# Revit family: Shower-Handshower-KOHLER-Statement-K-20998T_1
name_source: partatom
category: Plumbing Fixtures
units: mm (PartAtom-declared; Revit-internal decimal feet)

## family parameters
Cut with Voids When Loaded = No
Host = Face
Maintain Annotation Orientation = No
OmniClass Number = 23.31.17.00
OmniClass Title = Showers
Part Type = Normal
Room Calculation Point = No
Round Connector Dimension = Use Diameter
Shared = No

## types (2) — shared parameters
ADA Compliant = No
Assembly Code = D2010700
CW Connection = No
Cold Water Inlet = Cold Water Inlet
Date Modified = 03/01/2022
Default Elevation = 0"
Description = Ves low-flow handshower
Drain Included = No
Flow Rate = 2 GPM
HW Connection = Yes
Height = 10 7/16"
Hot Water Inlet = Tempered Water Inlet
Length = 3 3/8"
Manufacturer = KOHLER Co.
Master Format 2014 = 22 42 23
Master Format 2014 Name = Residential Showers
Material = Plastic
Pressure = 80.00 psi
Product Name = Statement
URL = http://www.kohler.com.cn
Vent Connection = No
Waste Connection = No
Waste Water Outlet = Waste Water Outlet
WaterSense Certified = No
Width = 4 15/16"

## per-type parameters (varying)
| type | Finish | Model | Secondary Finish | Type |
| CP-Polished Chrome | Kohler-Plastic-CP-Polished_Chrome | K-20998T-CP | Kohler-Plastic-0-White | 1 |
| BL-Matte Black | Kohler-Plastic-BL-Matte_Black | K-20998T-BL | Kohler-Plastic-58-Thunder_Grey | 2 |

## geometry (parser evidence)
native form markers: Sweep x6
no freeform markers — native parametric forms only
